# Revit family: FMV2-10 CDG
name_source: partatom
category: Mechanical Equipment
revit_build: Autodesk Revit 2017 (Build: 20160225_1515(x64)
units: mm (PartAtom-declared; Revit-internal decimal feet)

## family parameters
Always vertical = Yes
Cut with Voids When Loaded = No
OmniClass Number = 23.75.00.00
OmniClass Title = Climate Control (HVAC)
Part Type = Normal
Room Calculation Point = No
Round Connector Dimension = Use Diameter
Shared = No
Work Plane-Based = No

## types (1)
- FMV2-10 CDG
    Anchorage = 0.625" holes for 0.5" anchors (x4)
    Description = Multistage Variable Speed Duplex Booster Pump
    FLA = 55.9@208V/ 50.6@230V/ 25.3@460V
    Inlet Header Size = 4"
    Manufacturer = FlowTherm Systems
    Model = FMV2-10
    Outlet Header Size = 4"
    Phase = 3
    System Integration Panel (SIG) = NEMA-1; NEMA-3R; NEMA-4; NEMA-12
    URL = www.FLOWTHERM.com
    Voltage (Default) = 460.00 V
    Weight = 1,300 Lbs

## geometry (parser evidence)
native form markers: Sweep x3
no freeform markers — native parametric forms only
